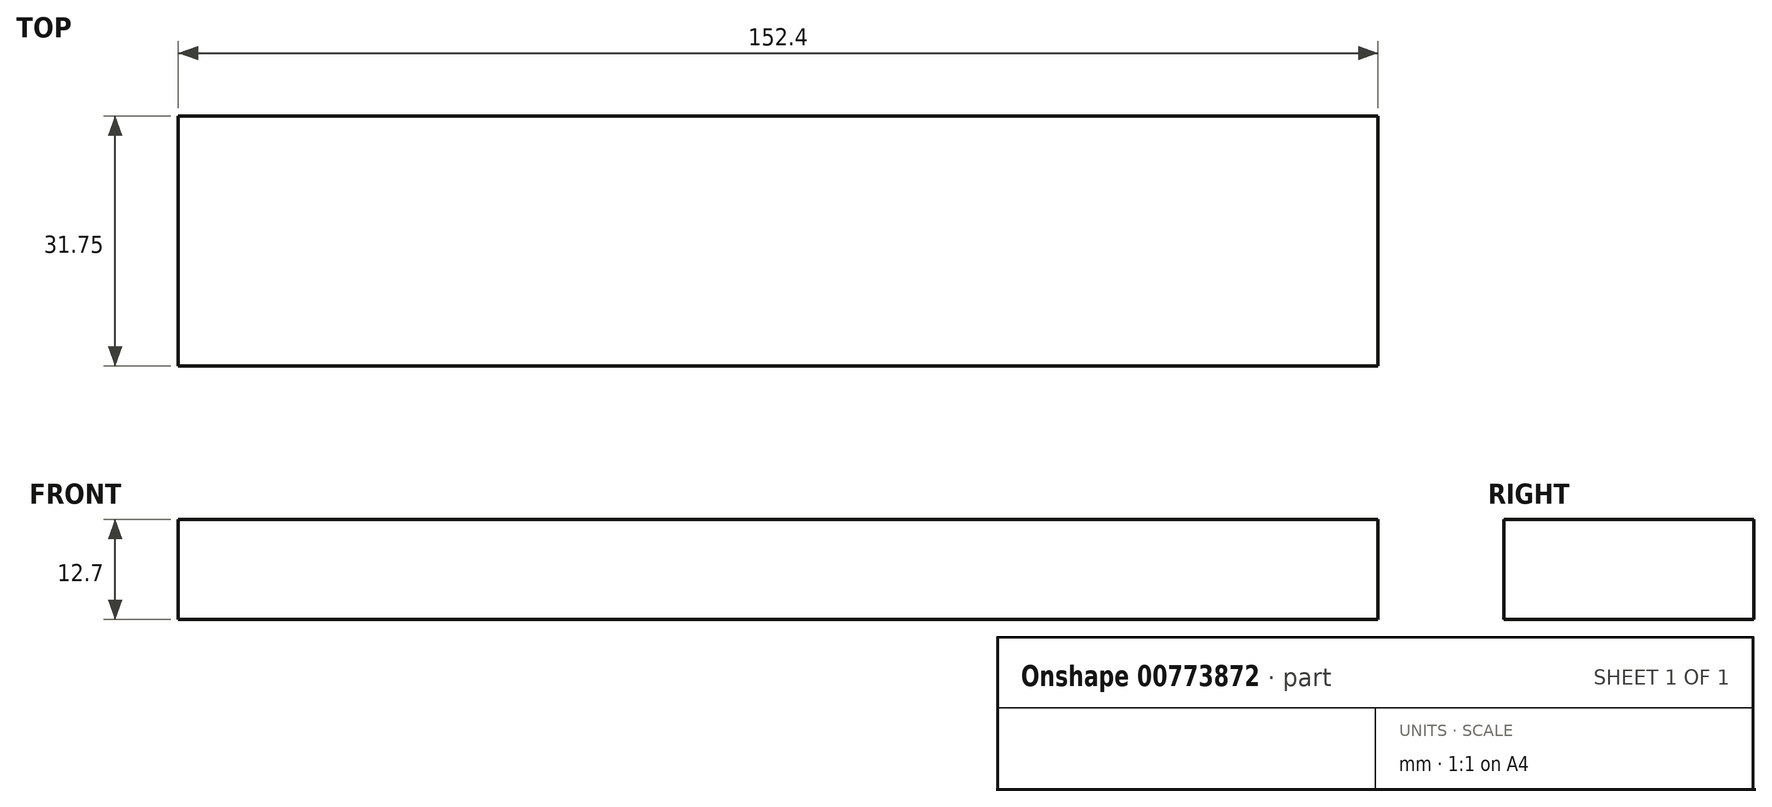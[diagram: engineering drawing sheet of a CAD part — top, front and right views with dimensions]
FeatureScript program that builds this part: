
annotation { "Feature Type Name" : "Feature", "Feature Type Description" : "" }
export const myFeature = defineFeature(function(context is Context, id is Id, definition is map)
    precondition{}
    {
        {
            var Q0;
            Q0=qCreatedBy(makeId("Top.planeOp"),FACE);
            var sketch = newSketch(context, id + "F0", { "sketchPlane" : qUnion([Q0])});
            skLineSegment(sketch, "E0.bottom", {"start": v(0, 0) * mm, "end": v(-152.4, 0) * mm});
            skLineSegment(sketch, "E0.top", {"start": v(0, 31.75) * mm, "end": v(-152.4, 31.75) * mm});
            skLineSegment(sketch, "E0.left", {"start": v(0, 0) * mm, "end": v(0, 31.75) * mm});
            skLineSegment(sketch, "E0.right", {"start": v(-152.4, 0) * mm, "end": v(-152.4, 31.75) * mm});
            skSolve(sketch);
        }
        {
            var Q0;
            Q0 = qSketchRegion(id + "F0", true);
            extrude(context, id + "F1", {"entities" : qUnion([Q0]), "depth" : 12.7 * mm, "offsetDistance" : 25.4 * mm});
        }
    });
